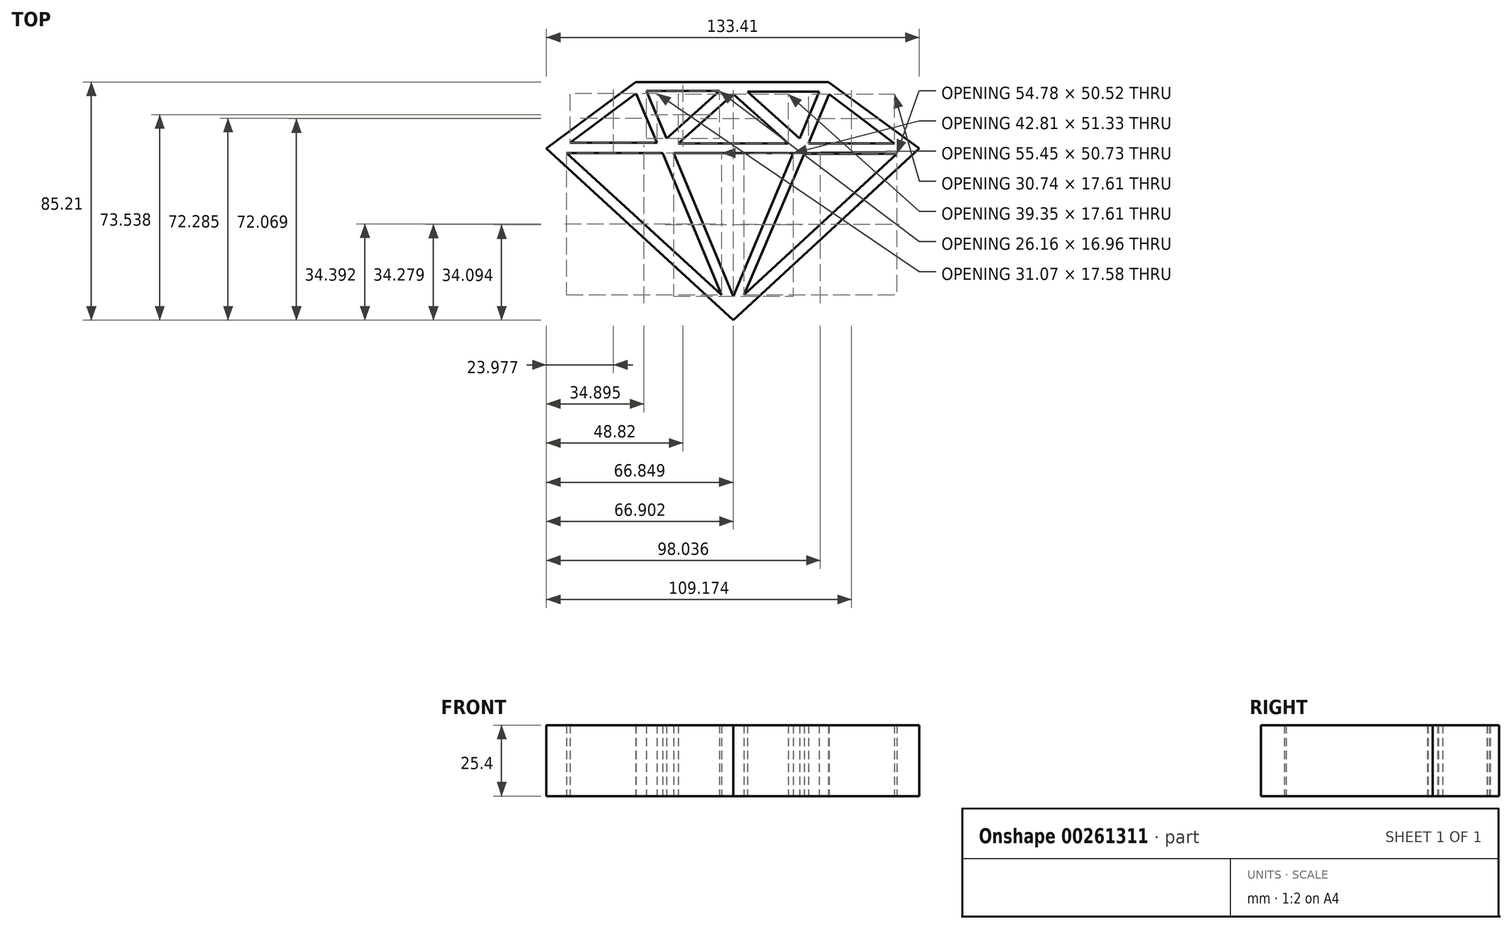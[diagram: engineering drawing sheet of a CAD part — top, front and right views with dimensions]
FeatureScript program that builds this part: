
annotation { "Feature Type Name" : "Feature", "Feature Type Description" : "" }
export const myFeature = defineFeature(function(context is Context, id is Id, definition is map)
    precondition{}
    {
        {
            var Q0;
            Q0=qCreatedBy(makeId("Top.planeOp"),FACE);
            var sketch = newSketch(context, id + "F0", { "sketchPlane" : qUnion([Q0])});
            skLineSegment(sketch, "E0", {"start": v(-66.81, 13.32) * mm, "end": v(-34.86, 37.04) * mm});
            skLineSegment(sketch, "E1", {"start": v(-58.37, 15.32) * mm, "end": v(-34.69, 32.9) * mm});
            skLineSegment(sketch, "E2", {"start": v(-58.37, 15.32) * mm, "end": v(-27.3, 15.32) * mm});
            skLineSegment(sketch, "E3", {"start": v(-34.69, 32.9) * mm, "end": v(-27.3, 15.32) * mm});
            skLineSegment(sketch, "E4", {"start": v(-31.07, 33.85) * mm, "end": v(-4.91, 33.85) * mm});
            skLineSegment(sketch, "E5", {"start": v(-31.07, 33.85) * mm, "end": v(-23.82, 16.9) * mm});
            skLineSegment(sketch, "E6", {"start": v(-23.82, 16.9) * mm, "end": v(-4.91, 33.85) * mm});
            skLineSegment(sketch, "E7", {"start": v(-19.64, 15.1) * mm, "end": v(0, 32.7) * mm});
            skLineSegment(sketch, "E8", {"start": v(-19.64, 15.1) * mm, "end": v(19.71, 15.1) * mm});
            skLineSegment(sketch, "E9", {"start": v(0, 32.7) * mm, "end": v(19.71, 15.1) * mm});
            skLineSegment(sketch, "E10", {"start": v(5.1, 33.6) * mm, "end": v(30.74, 33.6) * mm});
            skLineSegment(sketch, "E11", {"start": v(23.82, 16.9) * mm, "end": v(30.74, 33.6) * mm});
            skLineSegment(sketch, "E12", {"start": v(5.1, 33.6) * mm, "end": v(23.82, 16.9) * mm});
            skLineSegment(sketch, "E13", {"start": v(27, 15.1) * mm, "end": v(34.4, 32.7) * mm});
            skLineSegment(sketch, "E14", {"start": v(34.4, 32.7) * mm, "end": v(57.73, 15.1) * mm});
            skLineSegment(sketch, "E15", {"start": v(57.73, 15.1) * mm, "end": v(27, 15.1) * mm});
            skLineSegment(sketch, "E16", {"start": v(-59.64, 11.59) * mm, "end": v(-25.26, 11.59) * mm});
            skLineSegment(sketch, "E17", {"start": v(-59.64, 11.59) * mm, "end": v(-4.19, -39.14) * mm});
            skLineSegment(sketch, "E18", {"start": v(-25.26, 11.59) * mm, "end": v(-4.19, -39.14) * mm});
            skLineSegment(sketch, "E19", {"start": v(-21.31, 11.59) * mm, "end": v(21.5, 11.59) * mm});
            skLineSegment(sketch, "E20", {"start": v(-21.31, 11.59) * mm, "end": v(0, -39.74) * mm});
            skLineSegment(sketch, "E21", {"start": v(0, -39.74) * mm, "end": v(21.5, 11.59) * mm});
            skLineSegment(sketch, "E22", {"start": v(25.42, 11.37) * mm, "end": v(58.62, 11.37) * mm});
            skLineSegment(sketch, "E23", {"start": v(25.42, 11.37) * mm, "end": v(3.83, -39.15) * mm});
            skLineSegment(sketch, "E24", {"start": v(3.83, -39.15) * mm, "end": v(58.62, 11.37) * mm});
            skLineSegment(sketch, "E25", {"start": v(-34.86, 37.04) * mm, "end": v(34.15, 37.04) * mm});
            skLineSegment(sketch, "E26", {"start": v(34.15, 37.04) * mm, "end": v(66.6, 13.24) * mm});
            skLineSegment(sketch, "E27", {"start": v(66.6, 13.24) * mm, "end": v(0, -48.17) * mm});
            skLineSegment(sketch, "E28", {"start": v(0, -48.17) * mm, "end": v(-66.81, 13.32) * mm});
            skSolve(sketch);
        }
        {
            var Q0;
            Q0 = qSketchRegion(id + "F0", true);
            extrude(context, id + "F1", {"entities" : qUnion([Q0]), "depth" : 25.4 * mm});
        }
    });
